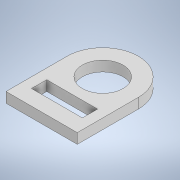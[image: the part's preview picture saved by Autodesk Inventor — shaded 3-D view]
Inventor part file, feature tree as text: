
AUTODESK INVENTOR PART (.ipt)
format: ipt  version: 2020 (Build 240168000, 168)  size: 110,080 bytes
history: native  units: mm
features: extrude x1, sketch x1
ambient origin geometry x8: Origin, YZ Plane, XZ Plane, XY Plane, X Axis, Y Axis, Z Axis, Center Point
bodies: Solid1 (feature_tree)
feature tree (2):
  extrude  "Extrusion1"  Depth=60.0mm
  sketch  "Sketch1"  dims[d0=70.0mm d1=60.0mm d4=40.0mm d6=50.0mm d7=15.0mm d8=15.0mm d9=10.0mm d10=10.0mm d11=0.0mm]
